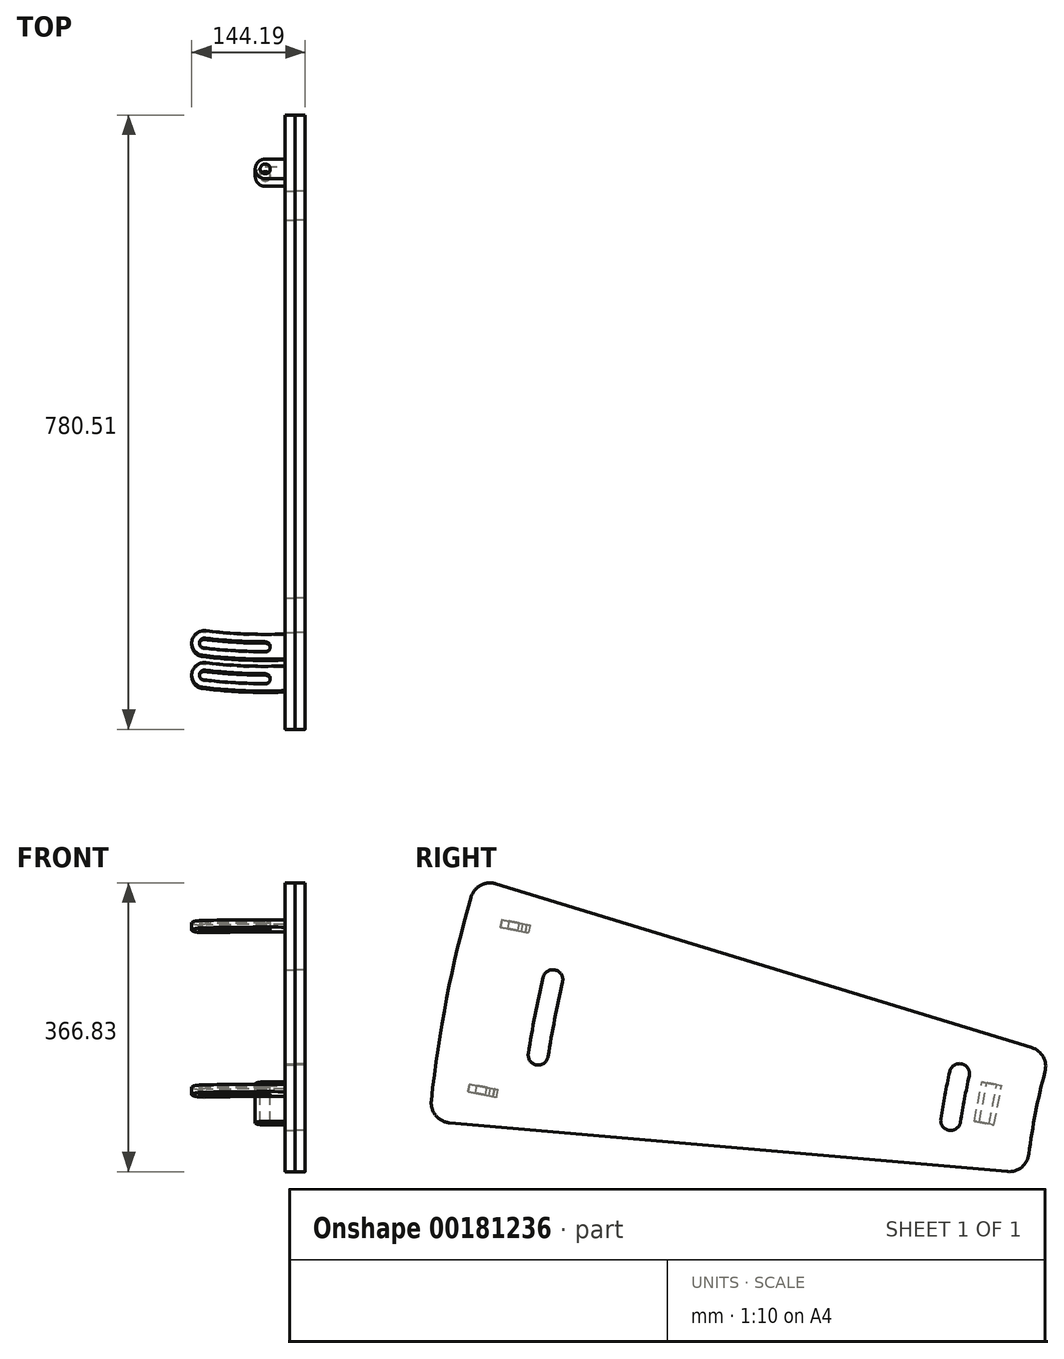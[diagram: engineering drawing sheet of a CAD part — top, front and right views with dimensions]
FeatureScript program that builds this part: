
annotation { "Feature Type Name" : "Feature", "Feature Type Description" : "" }
export const myFeature = defineFeature(function(context is Context, id is Id, definition is map)
    precondition{}
    {
        {
            var Q0;
            Q0=qCreatedBy(makeId("Right.planeOp"),FACE);
            var sketch = newSketch(context, id + "F0", { "sketchPlane" : qUnion([Q0])});
            skArc(sketch, "E0", {"start": v(-736.01, 197.3) * mm, "mid": v(-748, 145.4) * mm, "end": v(-756.33, 92.77) * mm});
            skLineSegment(sketch, "E1", {"start": v(0, 0) * mm, "end": v(-6.79, 0) * mm, "construction": true});
            skLineSegment(sketch, "E2", {"start": v(0, 0) * mm, "end": v(-1486.5, 288.95) * mm, "construction": true});
            skArc(sketch, "E3", {"start": v(-1465.3, 418.87) * mm, "mid": v(-1496, 290.8) * mm, "end": v(-1515.52, 160.55) * mm});
            skLineSegment(sketch, "E4", {"start": v(22.77, 0) * mm, "end": v(-18.63, 3.62) * mm});
            skArc(sketch, "E5", {"start": v(-844.59, 194.99) * mm, "mid": v(-850.72, 165.37) * mm, "end": v(-855.84, 135.55) * mm, "construction": true});
            skArc(sketch, "E6", {"start": v(-1361.2, 314.26) * mm, "mid": v(-1371.33, 266.56) * mm, "end": v(-1379.8, 218.54) * mm, "construction": true});
            skLineSegment(sketch, "E7.MirrorCS", {"start": v(21.1, -8.53) * mm, "end": v(-18.63, 3.62) * mm});
            skLineSegment(sketch, "E8.trimOffspring", {"start": v(-753.12, 228.18) * mm, "end": v(-1433.46, 436.18) * mm});
            skLineSegment(sketch, "E9.trimOffspring", {"start": v(-783.76, 70.56) * mm, "end": v(-1492.48, 132.57) * mm});
            skLineSegment(sketch, "E10.trimOffspring", {"start": v(-762, 0) * mm, "end": v(-1563.5, 0) * mm, "construction": true});
            skPoint(sketch, "E11.orphan", {"position": v(-1640.89, 499.6) * mm});
            skLineSegment(sketch, "E12", {"start": v(0, 0) * mm, "end": v(-1555.73, 246.4) * mm, "construction": true});
            skLineSegment(sketch, "E13", {"start": v(0, 0) * mm, "end": v(0, 0) * mm});
            skLineSegment(sketch, "E14.MirrorCS", {"start": v(0, 0) * mm, "end": v(-1534.75, 354.33) * mm, "construction": true});
            skArc(sketch, "E15.trimOffspring", {"start": v(-862.85, 77.48) * mm, "mid": v(-865.39, 38.78) * mm, "end": v(-866.23, 0) * mm, "construction": true});
            skArc(sketch, "E16.trimOffspring", {"start": v(-1391.5, 123.73) * mm, "mid": v(1371.33, -266.56) * mm, "end": v(-1336.54, 406.55) * mm, "construction": true});
            skArc(sketch, "E17.0.startCap", {"start": v(-1373.57, 317.11) * mm, "mid": v(-1358.34, 326.63) * mm, "end": v(-1348.82, 311.4) * mm});
            skArc(sketch, "E17.0.endCap", {"start": v(-1367.26, 216.55) * mm, "mid": v(-1381.79, 206) * mm, "end": v(-1392.34, 220.53) * mm});
            skArc(sketch, "E17.0.left", {"start": v(-1348.82, 311.4) * mm, "mid": v(-1358.87, 264.14) * mm, "end": v(-1367.26, 216.55) * mm});
            skArc(sketch, "E17.0.right", {"start": v(-1373.57, 317.11) * mm, "mid": v(-1383.8, 268.98) * mm, "end": v(-1392.34, 220.53) * mm});
            skArc(sketch, "E18.0.startCap", {"start": v(-856.98, 197.77) * mm, "mid": v(-841.8, 207.38) * mm, "end": v(-832.2, 192.2) * mm});
            skArc(sketch, "E18.0.endCap", {"start": v(-843.29, 133.62) * mm, "mid": v(-857.78, 123) * mm, "end": v(-868.4, 137.49) * mm});
            skArc(sketch, "E18.0.left", {"start": v(-832.2, 192.2) * mm, "mid": v(-838.24, 163) * mm, "end": v(-843.29, 133.62) * mm});
            skArc(sketch, "E18.0.right", {"start": v(-856.98, 197.77) * mm, "mid": v(-863.2, 167.73) * mm, "end": v(-868.4, 137.49) * mm});
            skPoint(sketch, "E19.visualSharp", {"position": v(-1457.99, 443.68) * mm});
            skArc(sketch, "E19.filletArc", {"start": v(-1433.46, 436.18) * mm, "mid": v(-1453.01, 434.2) * mm, "end": v(-1465.3, 418.87) * mm});
            skPoint(sketch, "E20.visualSharp", {"position": v(-729.28, 220.89) * mm});
            skArc(sketch, "E20.filletArc", {"start": v(-736.01, 197.3) * mm, "mid": v(-738.33, 216.2) * mm, "end": v(-753.12, 228.18) * mm});
            skPoint(sketch, "E21.visualSharp", {"position": v(-758.92, 68.39) * mm});
            skArc(sketch, "E21.filletArc", {"start": v(-783.76, 70.56) * mm, "mid": v(-765.56, 76.13) * mm, "end": v(-756.33, 92.77) * mm});
            skPoint(sketch, "E22.newPointA", {"position": v(-1708.56, 151.47) * mm});
            skArc(sketch, "E22.filletArc", {"start": v(-1515.52, 160.55) * mm, "mid": v(-1509.87, 141.72) * mm, "end": v(-1492.48, 132.57) * mm});
            skSolve(sketch);
        }
        {
            var Q0;
            Q0=makeQuery(id+"F0.imprint","IMPRINT",FACE,{"disambiguationData":[TD([[makeQuery(id+"F0.imprint","IMPRINT",EDGE,{"derivedFrom":sQuery(id+"F0.wireOp",EDGE,"E0")}),-1.0]])]});
            var Q1;
            Q1=makeQuery(id+"F0.imprint","IMPRINT",FACE,{"disambiguationData":[TD([[makeQuery(id+"F0.imprint","IMPRINT",EDGE,{"derivedFrom":sQuery(id+"F0.wireOp",EDGE,"E17.0.startCap")}),-1.0]])]});
            var Q2;
            Q2=makeQuery(id+"F0.imprint","IMPRINT",FACE,{"disambiguationData":[TD([[makeQuery(id+"F0.imprint","IMPRINT",EDGE,{"derivedFrom":sQuery(id+"F0.wireOp",EDGE,"E18.0.startCap")}),-1.0]])]});
            extrude(context, id + "F1", {"entities" : qUnion([Q0, Q1, Q2]), "oppositeDirection" : true, "depth" : 12.7 * mm});
        }
        {
            var Q0;
            Q0=makeQuery(id+"F0.imprint","IMPRINT",FACE,{"disambiguationData":[TD([[makeQuery(id+"F0.imprint","IMPRINT",EDGE,{"derivedFrom":sQuery(id+"F0.wireOp",EDGE,"E17.0.startCap")}),-1.0]])]});
            var Q1;
            Q1=makeQuery(id+"F0.imprint","IMPRINT",FACE,{"disambiguationData":[TD([[makeQuery(id+"F0.imprint","IMPRINT",EDGE,{"derivedFrom":sQuery(id+"F0.wireOp",EDGE,"E18.0.startCap")}),-1.0]])]});
            extrude(context, id + "F2", {"entities" : qUnion([Q0, Q1]), "depth" : 12.7 * mm});
        }
        {
            var Q0;
            Q0=makeQuery(id+"F2.opExtrude","CAP_FACE",FACE,{"disambiguationData":[OSD([sQuery(id+"F0.wireOp",EDGE,"E17.0.startCap"),sQuery(id+"F0.wireOp",EDGE,"E17.0.endCap"),sQuery(id+"F0.wireOp",EDGE,"E17.0.left"),sQuery(id+"F0.wireOp",EDGE,"E17.0.right")])],"isStart":false});
            var sketch = newSketch(context, id + "F3", { "sketchPlane" : qUnion([Q0])});
            skPoint(sketch, "E23", {"position": v(-1361.2, 314.26) * mm});
            skPoint(sketch, "E24", {"position": v(-1379.8, 218.54) * mm});
            skArc(sketch, "E25.0.0", {"start": v(-832.2, 192.2) * mm, "mid": v(-841.8, 207.38) * mm, "end": v(-856.98, 197.77) * mm, "construction": true});
            skArc(sketch, "E25.0.1", {"start": v(-856.98, 197.77) * mm, "mid": v(-863.2, 167.73) * mm, "end": v(-868.4, 137.49) * mm, "construction": true});
            skArc(sketch, "E25.0.2", {"start": v(-868.4, 137.49) * mm, "mid": v(-857.78, 123) * mm, "end": v(-843.29, 133.62) * mm, "construction": true});
            skArc(sketch, "E25.0.3", {"start": v(-843.29, 133.62) * mm, "mid": v(-838.24, 163) * mm, "end": v(-832.2, 192.2) * mm, "construction": true});
            skSolve(sketch);
        }
        {
            var Q0;
            Q0=sQuery(id+"F3.wireOp",VERTEX,"E23");
            var Q1;
            Q1=sQuery(id+"F3.wireOp",VERTEX,"E24");
            var Q2;
            Q2=sQuery(id+"F3.wireOp",VERTEX,"E25.0.0.center");
            var Q3;
            Q3=sQuery(id+"F3.wireOp",VERTEX,"E25.0.2.center");
            var Q4;
            Q4=makeQuery(id+"F1.opExtrude","SWEPT_BODY",BODY,{"disambiguationData":[OSD([sQuery(id+"F0.wireOp",EDGE,"E0"),sQuery(id+"F0.wireOp",EDGE,"E3"),sQuery(id+"F0.wireOp",EDGE,"E8.trimOffspring"),sQuery(id+"F0.wireOp",EDGE,"E9.trimOffspring"),sQuery(id+"F0.wireOp",EDGE,"E19.filletArc"),sQuery(id+"F0.wireOp",EDGE,"E20.filletArc"),sQuery(id+"F0.wireOp",EDGE,"E21.filletArc"),sQuery(id+"F0.wireOp",EDGE,"E22.filletArc")])]});
            hole(context, id + "F4", {"style" : HoleStyle.SIMPLE, "endStyle" : HoleEndStyle.THROUGH, "standardTappedOrClearance" : lookupTablePath({ "standard" : "ANSI", "fit" : "Normal (ASME)", "size" : "5/8", "type" : "Clearance" }), "standardBlindInLast" : lookupTablePath({ "fit" : "Free", "standard" : "ANSI", "size" : "5/8", "type" : "Clearance" }), "holeDiameter" : 16.67 * mm, "locations" : qUnion([Q0, Q1, Q2, Q3]), "scope" : qUnion([Q4]), "isTappedThrough" : true});
        }
        {
            var Q0;
            Q0=makeQuery(id+"F1.opExtrude","SWEPT_FACE",FACE,{"disambiguationData":[OSD([sQuery(id+"F0.wireOp",EDGE,"E9.trimOffspring")])]});
            var Q1;
            Q1=makeQuery(id+"F1.opExtrude","SWEPT_FACE",FACE,{"disambiguationData":[OSD([sQuery(id+"F0.wireOp",EDGE,"E8.trimOffspring")])]});
            cPlane(context, id + "F5", {"entities" : qUnion([Q0, Q1]), "cplaneType" : CPlaneType.MID_PLANE, "offset" : 25.4 * mm, "width" : 152.4 * mm, "height" : 152.4 * mm});
        }
        {
            var Q0;
            Q0=qCreatedBy(id+"F5.planeOp",FACE);
            var sketch = newSketch(context, id + "F6", { "sketchPlane" : qUnion([Q0])});
            skLineSegment(sketch, "E26.0", {"start": v(-12.7, 782.82) * mm, "end": v(-12.7, 1490.35) * mm, "construction": true});
            skLineSegment(sketch, "E27", {"start": v(0, 760.08) * mm, "end": v(-12.7, 760.08) * mm, "construction": true});
            skLineSegment(sketch, "E28", {"start": v(-12.7, 760.08) * mm, "end": v(-65.49, 760.08) * mm, "construction": true});
            skLineSegment(sketch, "E29.0", {"start": v(-12.7, 823.58) * mm, "end": v(-38.1, 823.58) * mm, "construction": true});
            skCircle(sketch, "E30", {"center": v(-38.1, 823.58) * mm, "radius": 6.35 * mm});
            skCircle(sketch, "E31", {"center": v(-38.1, 823.58) * mm, "radius": 12.7 * mm});
            skLineSegment(sketch, "E32", {"start": v(-38.1, 829.93) * mm, "end": v(-38.1, 836.28) * mm});
            skLineSegment(sketch, "E33", {"start": v(-38.1, 836.28) * mm, "end": v(-12.7, 836.28) * mm});
            skLineSegment(sketch, "E34", {"start": v(-38.1, 817.23) * mm, "end": v(-38.1, 810.88) * mm});
            skLineSegment(sketch, "E35", {"start": v(-38.1, 810.88) * mm, "end": v(-12.7, 810.88) * mm});
            skLineSegment(sketch, "E36", {"start": v(-12.7, 810.88) * mm, "end": v(-12.7, 836.28) * mm});
            skSolve(sketch);
        }
        {
            var Q0;
            Q0=qSketchRegion(id+"F6",true);
            extrude(context, id + "F7", {"entities" : qUnion([Q0]), "operationType" : NewBodyOperationType.ADD, "endBound" : BoundingType.SYMMETRIC, "depth" : 50.8 * mm});
        }
        {
            var Q0;
            Q0=qCreatedBy(id+"F5.planeOp",FACE);
            cPlane(context, id + "F8", {"entities" : qUnion([Q0]), "cplaneType" : CPlaneType.OFFSET, "offset" : 101.6 * mm, "width" : 152.4 * mm, "height" : 152.4 * mm});
        }
        {
            var Q0;
            Q0=qCreatedBy(id+"F8.planeOp",FACE);
            var sketch = newSketch(context, id + "F9", { "sketchPlane" : qUnion([Q0])});
            skLineSegment(sketch, "E37.0.0", {"start": v(-12.7, 836.28) * mm, "end": v(-38.1, 836.28) * mm, "construction": true});
            skArc(sketch, "E37.0.1", {"start": v(-38.1, 836.28) * mm, "mid": v(-50.8, 823.58) * mm, "end": v(-38.1, 810.88) * mm, "construction": true});
            skLineSegment(sketch, "E37.0.2", {"start": v(-38.1, 810.88) * mm, "end": v(-12.7, 810.88) * mm, "construction": true});
            skLineSegment(sketch, "E37.0.3", {"start": v(-12.7, 810.88) * mm, "end": v(-12.7, 836.28) * mm, "construction": true});
            skLineSegment(sketch, "E38.0", {"start": v(0, 1518.3) * mm, "end": v(0, 1524) * mm, "construction": true});
            skLineSegment(sketch, "E38.3", {"start": v(0, 1490.35) * mm, "end": v(0, 1518.3) * mm, "construction": true});
            skLineSegment(sketch, "E38.4", {"start": v(0, 1383.45) * mm, "end": v(0, 1408.84) * mm, "construction": true});
            skLineSegment(sketch, "E38.5", {"start": v(0, 1518.3) * mm, "end": v(0, 1490.35) * mm, "construction": true});
            skLineSegment(sketch, "E38.6", {"start": v(0, 1408.84) * mm, "end": v(0, 1383.45) * mm, "construction": true});
            skLineSegment(sketch, "E38.10", {"start": v(12.7, 1383.45) * mm, "end": v(12.7, 1408.84) * mm, "construction": true});
            skLineSegment(sketch, "E38.11", {"start": v(-12.7, 1490.35) * mm, "end": v(0, 1490.35) * mm, "construction": true});
            skLineSegment(sketch, "E38.12", {"start": v(-12.7, 1518.3) * mm, "end": v(-12.7, 1490.35) * mm, "construction": true});
            skLineSegment(sketch, "E38.13", {"start": v(-12.7, 782.82) * mm, "end": v(-12.7, 836.28) * mm, "construction": true});
            skLineSegment(sketch, "E38.14", {"start": v(-12.7, 1518.3) * mm, "end": v(-12.7, 1524) * mm, "construction": true});
            skLineSegment(sketch, "E38.15", {"start": v(0, 1389.55) * mm, "end": v(0, -1397) * mm, "construction": true});
            skLineSegment(sketch, "E38.17", {"start": v(12.7, 1408.84) * mm, "end": v(0, 1408.84) * mm, "construction": true});
            skLineSegment(sketch, "E38.18", {"start": v(-12.7, 1518.3) * mm, "end": v(0, 1518.3) * mm, "construction": true});
            skLineSegment(sketch, "E38.19", {"start": v(0, 1518.3) * mm, "end": v(0, 1524) * mm, "construction": true});
            skLineSegment(sketch, "E38.20", {"start": v(-12.7, 1387.82) * mm, "end": v(-12.7, 1404.48) * mm, "construction": true});
            skLineSegment(sketch, "E38.21", {"start": v(12.7, 1401.9) * mm, "end": v(12.7, 1390.4) * mm, "construction": true});
            skLineSegment(sketch, "E38.22", {"start": v(12.7, 1401.9) * mm, "end": v(12.7, 1390.4) * mm, "construction": true});
            skLineSegment(sketch, "E38.23", {"start": v(-12.7, 1490.35) * mm, "end": v(-12.7, 1518.3) * mm, "construction": true});
            skLineSegment(sketch, "E38.24", {"start": v(-12.7, 1387.82) * mm, "end": v(-12.7, 1404.48) * mm, "construction": true});
            skLineSegment(sketch, "E38.25", {"start": v(12.7, 1408.84) * mm, "end": v(12.7, 1383.45) * mm, "construction": true});
            skLineSegment(sketch, "E38.26", {"start": v(-12.7, 1518.3) * mm, "end": v(0, 1518.3) * mm, "construction": true});
            skLineSegment(sketch, "E38.27", {"start": v(-12.7, 782.82) * mm, "end": v(-12.7, 1387.82) * mm, "construction": true});
            skLineSegment(sketch, "E38.29", {"start": v(-12.7, 1490.35) * mm, "end": v(0, 1490.35) * mm, "construction": true});
            skLineSegment(sketch, "E38.30", {"start": v(0, 1518.3) * mm, "end": v(0, 1490.35) * mm, "construction": true});
            skLineSegment(sketch, "E38.31", {"start": v(12.7, 1383.46) * mm, "end": v(0, 1383.46) * mm, "construction": true});
            skLineSegment(sketch, "E38.32", {"start": v(12.7, 1408.84) * mm, "end": v(12.7, 1409.7) * mm, "construction": true});
            skLineSegment(sketch, "E38.33", {"start": v(0, 1396.15) * mm, "end": v(0, 1397) * mm, "construction": true});
            skLineSegment(sketch, "E38.34", {"start": v(0, 1383.46) * mm, "end": v(0, 1384.3) * mm, "construction": true});
            skLineSegment(sketch, "E38.35", {"start": v(0, 1408.84) * mm, "end": v(0, 1409.7) * mm, "construction": true});
            skLineSegment(sketch, "E38.37", {"start": v(12.7, 1383.46) * mm, "end": v(0, 1383.46) * mm, "construction": true});
            skLineSegment(sketch, "E38.38", {"start": v(12.7, 1408.84) * mm, "end": v(0, 1408.84) * mm, "construction": true});
            skLineSegment(sketch, "E38.39", {"start": v(0, 1490.35) * mm, "end": v(0, 1518.3) * mm, "construction": true});
            skLineSegment(sketch, "E38.40", {"start": v(12.7, 1383.46) * mm, "end": v(12.7, 1384.3) * mm, "construction": true});
            skLineSegment(sketch, "E38.41", {"start": v(0, 1383.45) * mm, "end": v(0, 1408.84) * mm, "construction": true});
            skLineSegment(sketch, "E38.42", {"start": v(0, 1408.84) * mm, "end": v(0, 1409.7) * mm, "construction": true});
            skLineSegment(sketch, "E38.43", {"start": v(0, 1383.46) * mm, "end": v(0, 1384.3) * mm, "construction": true});
            skLineSegment(sketch, "E38.44", {"start": v(0, 1408.84) * mm, "end": v(0, 1383.45) * mm, "construction": true});
            skArc(sketch, "E39", {"start": v(0, 189.72) * mm, "mid": v(596.87, 829.93) * mm, "end": v(-12.7, 1458.07) * mm, "construction": true});
            skLineSegment(sketch, "E40", {"start": v(-38.1, 823.58) * mm, "end": v(-38.1, 1674.01) * mm, "construction": true});
            skLineSegment(sketch, "E41", {"start": v(-38.1, 823.58) * mm, "end": v(-115.49, 1453.84) * mm, "construction": true});
            skArc(sketch, "E42", {"start": v(-38.1, 1452.23) * mm, "mid": v(-31.75, 1458.58) * mm, "end": v(-38.1, 1464.93) * mm});
            skArc(sketch, "E43", {"start": v(-116.26, 1460.14) * mm, "mid": v(-121.79, 1453.07) * mm, "end": v(-114.71, 1447.54) * mm});
            skArc(sketch, "E44.trimOffspring", {"start": v(-31.75, 1458.54) * mm, "mid": v(-76.87, 1457.4) * mm, "end": v(-121.79, 1453.04) * mm, "construction": true});
            skArc(sketch, "E45.0", {"start": v(-38.1, 1464.93) * mm, "mid": v(-77.25, 1463.73) * mm, "end": v(-116.26, 1460.14) * mm});
            skArc(sketch, "E46.0", {"start": v(-38.1, 1452.23) * mm, "mid": v(-76.48, 1451.05) * mm, "end": v(-114.71, 1447.54) * mm});
            skLineSegment(sketch, "E47.0.0", {"start": v(0, 782.82) * mm, "end": v(0, 1409.7) * mm});
            skLineSegment(sketch, "E47.0.1", {"start": v(0, 1490.35) * mm, "end": v(-12.7, 1490.35) * mm});
            skLineSegment(sketch, "E47.0.2", {"start": v(-12.7, 1474.08) * mm, "end": v(-12.7, 1458.07) * mm});
            skLineSegment(sketch, "E47.0.3", {"start": v(-12.7, 782.82) * mm, "end": v(0, 782.82) * mm});
            skArc(sketch, "E48.0", {"start": v(-117.44, 1469.72) * mm, "mid": v(-131.37, 1451.9) * mm, "end": v(-113.54, 1437.96) * mm});
            skArc(sketch, "E49.0", {"start": v(-12.7, 1442.05) * mm, "mid": v(-63.2, 1442.06) * mm, "end": v(-113.54, 1437.96) * mm});
            skArc(sketch, "E50.0", {"start": v(-12.7, 1474.08) * mm, "mid": v(-68.4, 1473.87) * mm, "end": v(-123.9, 1468.9) * mm});
            skPoint(sketch, "E38.8.start.orphan", {"position": v(0, 748) * mm});
            skLineSegment(sketch, "E51.trimOffspring", {"start": v(-12.7, 1442.05) * mm, "end": v(-12.7, 1458.07) * mm, "construction": true});
            skLineSegment(sketch, "E52.trimOffspring", {"start": v(-12.7, 1442.05) * mm, "end": v(-12.7, 1474.08) * mm});
            skLineSegment(sketch, "E53.trimOffspring", {"start": v(-12.7, 1404.48) * mm, "end": v(-12.7, 782.82) * mm});
            skSolve(sketch);
        }
        {
            var Q0;
            Q0=qSketchRegion(id+"F9",true);
            extrude(context, id + "F10", {"entities" : qUnion([Q0]), "depth" : 9.65 * mm});
        }
        {
            var Q0;
            Q0=makeQuery(id+"F10.opExtrude","SWEPT_BODY",BODY,{"disambiguationData":[OSD([sQuery(id+"F9.wireOp",EDGE,"E42"),sQuery(id+"F9.wireOp",EDGE,"E43"),sQuery(id+"F9.wireOp",EDGE,"E45.0"),sQuery(id+"F9.wireOp",EDGE,"E46.0"),sQuery(id+"F9.wireOp",EDGE,"E48.0"),sQuery(id+"F9.wireOp",EDGE,"E49.0"),sQuery(id+"F9.wireOp",EDGE,"E50.0"),sQuery(id+"F9.wireOp",EDGE,"E52.trimOffspring")])]});
            var Q1;
            Q1=qCreatedBy(id+"F5.planeOp",FACE);
            mirror(context, id + "F11", {"entities" : qUnion([Q0]), "mirrorPlane" : qUnion([Q1])});
        }
        {
            var Q0;
            Q0=makeQuery(id+"F2.opExtrude","CAP_FACE",FACE,{"disambiguationData":[OSD([sQuery(id+"F0.wireOp",EDGE,"E18.0.startCap"),sQuery(id+"F0.wireOp",EDGE,"E18.0.endCap"),sQuery(id+"F0.wireOp",EDGE,"E18.0.left"),sQuery(id+"F0.wireOp",EDGE,"E18.0.right")])],"isStart":false});
            var sketch = newSketch(context, id + "F12", { "sketchPlane" : qUnion([Q0])});
            skArc(sketch, "E54.0.0", {"start": v(-832.2, 192.2) * mm, "mid": v(-841.8, 207.38) * mm, "end": v(-856.98, 197.77) * mm, "construction": true});
            skArc(sketch, "E54.0.1", {"start": v(-856.98, 197.77) * mm, "mid": v(-863.2, 167.73) * mm, "end": v(-868.4, 137.49) * mm, "construction": true});
            skArc(sketch, "E54.0.2", {"start": v(-868.4, 137.49) * mm, "mid": v(-857.78, 123) * mm, "end": v(-843.29, 133.62) * mm, "construction": true});
            skArc(sketch, "E54.0.3", {"start": v(-843.29, 133.62) * mm, "mid": v(-838.24, 163) * mm, "end": v(-832.2, 192.2) * mm, "construction": true});
            skSolve(sketch);
        }
        {
            var Q0;
            Q0=sQuery(id+"F12.wireOp",VERTEX,"E54.0.0.center");
            var Q1;
            Q1=sQuery(id+"F12.wireOp",VERTEX,"E54.0.2.center");
            var Q2;
            Q2=makeQuery(id+"F2.opExtrude","SWEPT_BODY",BODY,{"disambiguationData":[OSD([sQuery(id+"F0.wireOp",EDGE,"E18.0.startCap"),sQuery(id+"F0.wireOp",EDGE,"E18.0.endCap"),sQuery(id+"F0.wireOp",EDGE,"E18.0.left"),sQuery(id+"F0.wireOp",EDGE,"E18.0.right")])]});
            hole(context, id + "F13", {"style" : HoleStyle.SIMPLE, "endStyle" : HoleEndStyle.THROUGH, "standardTappedOrClearance" : lookupTablePath({ "standard" : "ANSI", "fit" : "Normal (ASME)", "size" : "5/8", "type" : "Clearance" }), "standardBlindInLast" : lookupTablePath({ "fit" : "Free", "standard" : "ANSI", "size" : "5/8", "type" : "Clearance" }), "holeDiameter" : 16.67 * mm, "locations" : qUnion([Q0, Q1]), "scope" : qUnion([Q2]), "isTappedThrough" : true});
        }
        {
            var Q0;
            Q0=makeQuery(id+"F2.opExtrude","CAP_FACE",FACE,{"disambiguationData":[OSD([sQuery(id+"F0.wireOp",EDGE,"E17.0.startCap"),sQuery(id+"F0.wireOp",EDGE,"E17.0.endCap"),sQuery(id+"F0.wireOp",EDGE,"E17.0.left"),sQuery(id+"F0.wireOp",EDGE,"E17.0.right")])],"isStart":false});
            var sketch = newSketch(context, id + "F14", { "sketchPlane" : qUnion([Q0])});
            skArc(sketch, "E55.0.0", {"start": v(-1348.82, 311.4) * mm, "mid": v(-1358.34, 326.63) * mm, "end": v(-1373.57, 317.11) * mm, "construction": true});
            skArc(sketch, "E55.0.1", {"start": v(-1373.57, 317.11) * mm, "mid": v(-1383.8, 268.98) * mm, "end": v(-1392.34, 220.53) * mm, "construction": true});
            skArc(sketch, "E55.0.2", {"start": v(-1392.34, 220.53) * mm, "mid": v(-1381.79, 206) * mm, "end": v(-1367.26, 216.55) * mm, "construction": true});
            skArc(sketch, "E55.0.3", {"start": v(-1367.26, 216.55) * mm, "mid": v(-1358.87, 264.14) * mm, "end": v(-1348.82, 311.4) * mm, "construction": true});
            skSolve(sketch);
        }
        {
            var Q0;
            Q0=sQuery(id+"F14.wireOp",VERTEX,"E55.0.0.center");
            var Q1;
            Q1=sQuery(id+"F14.wireOp",VERTEX,"E55.0.2.center");
            var Q2;
            Q2=makeQuery(id+"F2.opExtrude","SWEPT_BODY",BODY,{"disambiguationData":[OSD([sQuery(id+"F0.wireOp",EDGE,"E17.0.startCap"),sQuery(id+"F0.wireOp",EDGE,"E17.0.endCap"),sQuery(id+"F0.wireOp",EDGE,"E17.0.left"),sQuery(id+"F0.wireOp",EDGE,"E17.0.right")])]});
            hole(context, id + "F15", {"style" : HoleStyle.SIMPLE, "endStyle" : HoleEndStyle.THROUGH, "standardTappedOrClearance" : lookupTablePath({ "standard" : "ANSI", "fit" : "Normal (ASME)", "size" : "5/8", "type" : "Clearance" }), "standardBlindInLast" : lookupTablePath({ "fit" : "Free", "standard" : "ANSI", "size" : "5/8", "type" : "Clearance" }), "holeDiameter" : 16.67 * mm, "locations" : qUnion([Q0, Q1]), "scope" : qUnion([Q2]), "isTappedThrough" : true});
        }
    });
